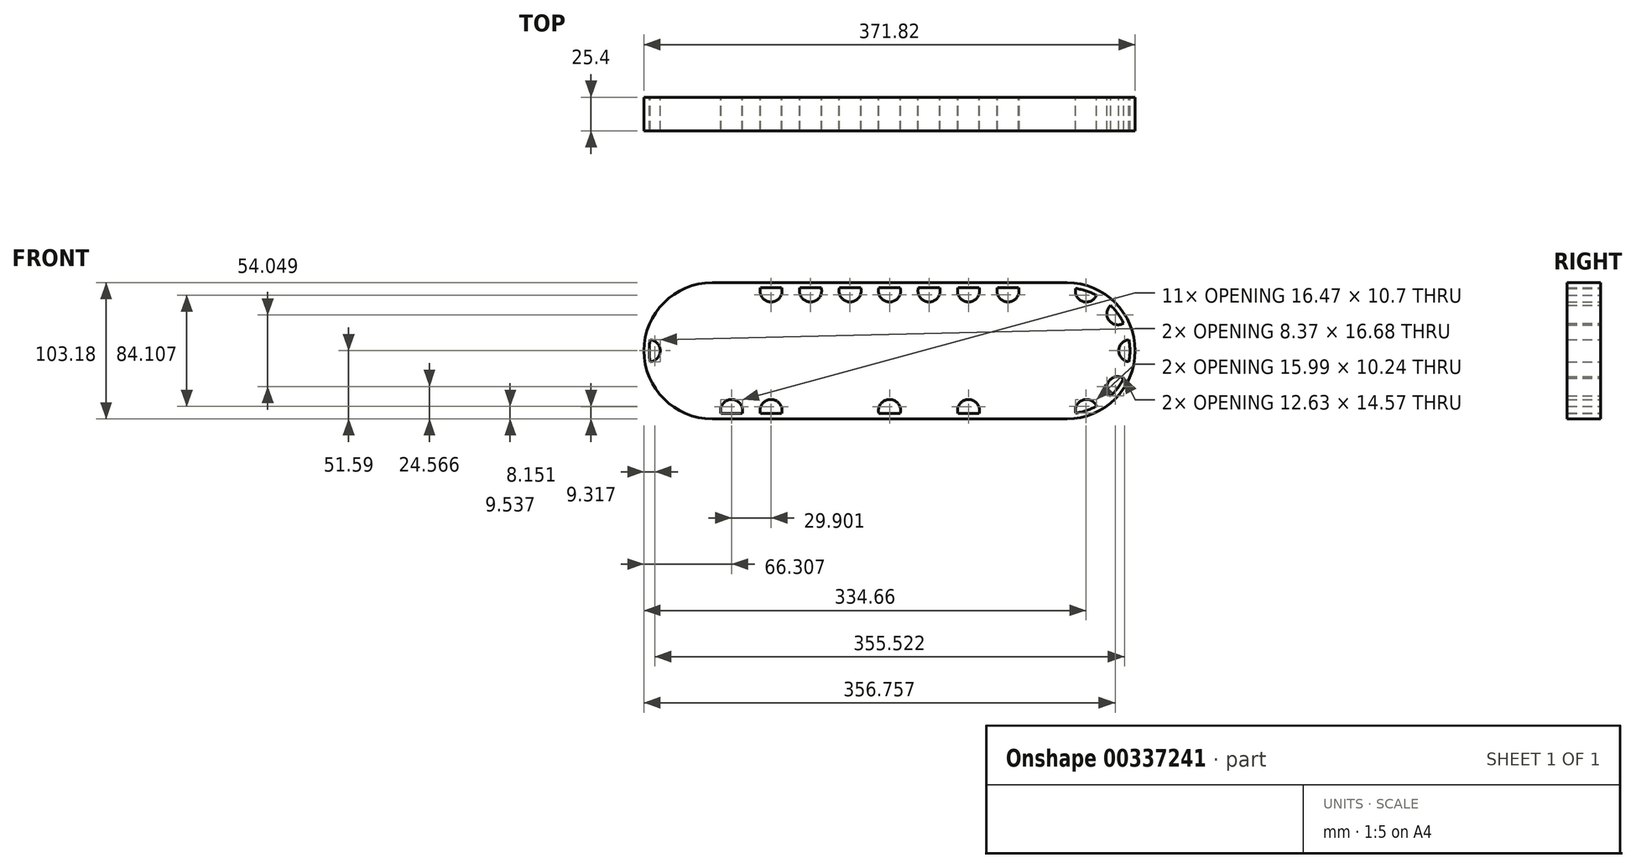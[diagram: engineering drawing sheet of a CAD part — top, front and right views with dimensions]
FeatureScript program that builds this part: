
annotation { "Feature Type Name" : "Feature", "Feature Type Description" : "" }
export const myFeature = defineFeature(function(context is Context, id is Id, definition is map)
    precondition{}
    {
        {
            var Q0;
            Q0=qCreatedBy(makeId("Front.planeOp"),FACE);
            var sketch = newSketch(context, id + "F0", { "sketchPlane" : qUnion([Q0])});
            skCircle(sketch, "E0", {"center": v(0, 0) * mm, "radius": 15.88 * mm});
            skCircle(sketch, "E1", {"center": v(0, 0) * mm, "radius": 25.4 * mm});
            skCircle(sketch, "E2", {"center": v(0, 0) * mm, "radius": 38.1 * mm});
            skArc(sketch, "E3", {"start": v(-23.03, 41.69) * mm, "mid": v(-28, 38.53) * mm, "end": v(-32.53, 34.79) * mm});
            skCircle(sketch, "E4", {"center": v(0, 0) * mm, "radius": 9.53 * mm});
            skLineSegment(sketch, "E5", {"start": v(-7.62, 37.33) * mm, "end": v(-5.87, 47.26) * mm});
            skLineSegment(sketch, "E6", {"start": v(5.87, 47.26) * mm, "end": v(7.62, 37.33) * mm});
            skLineSegment(sketch, "E7.1.0", {"start": v(-28.1, 25.72) * mm, "end": v(-32.53, 34.79) * mm});
            skLineSegment(sketch, "E7.1.1", {"start": v(-23.03, 41.69) * mm, "end": v(-15.78, 34.68) * mm});
            skLineSegment(sketch, "E7.2.0", {"start": v(-37.86, 4.29) * mm, "end": v(-46.76, 9.02) * mm});
            skLineSegment(sketch, "E7.2.1", {"start": v(-43.14, 20.19) * mm, "end": v(-33.15, 18.78) * mm});
            skLineSegment(sketch, "E8.1.3.0", {"start": v(-33.15, -18.78) * mm, "end": v(-43.14, -20.19) * mm});
            skLineSegment(sketch, "E8.3.3.0", {"start": v(-46.76, -9.02) * mm, "end": v(-37.86, -4.29) * mm});
            skLineSegment(sketch, "E8.1.4.0", {"start": v(-15.78, -34.68) * mm, "end": v(-23.03, -41.69) * mm});
            skLineSegment(sketch, "E8.3.4.0", {"start": v(-32.53, -34.79) * mm, "end": v(-28.1, -25.72) * mm});
            skLineSegment(sketch, "E8.1.5.0", {"start": v(7.62, -37.33) * mm, "end": v(5.87, -47.26) * mm});
            skLineSegment(sketch, "E8.3.5.0", {"start": v(-5.87, -47.26) * mm, "end": v(-7.62, -37.33) * mm});
            skLineSegment(sketch, "E8.1.6.0", {"start": v(28.1, -25.72) * mm, "end": v(32.53, -34.79) * mm});
            skLineSegment(sketch, "E8.3.6.0", {"start": v(23.03, -41.69) * mm, "end": v(15.78, -34.68) * mm});
            skLineSegment(sketch, "E8.1.7.0", {"start": v(37.86, -4.29) * mm, "end": v(46.76, -9.02) * mm});
            skLineSegment(sketch, "E8.3.7.0", {"start": v(43.14, -20.19) * mm, "end": v(33.15, -18.78) * mm});
            skLineSegment(sketch, "E8.1.8.0", {"start": v(33.15, 18.78) * mm, "end": v(43.14, 20.19) * mm});
            skLineSegment(sketch, "E8.3.8.0", {"start": v(46.76, 9.02) * mm, "end": v(37.86, 4.29) * mm});
            skLineSegment(sketch, "E8.1.9.0", {"start": v(15.78, 34.68) * mm, "end": v(23.03, 41.69) * mm});
            skLineSegment(sketch, "E8.3.9.0", {"start": v(32.53, 34.79) * mm, "end": v(28.1, 25.72) * mm});
            skArc(sketch, "E9.trimOffspring", {"start": v(5.87, 47.26) * mm, "mid": v(0, 47.63) * mm, "end": v(-5.87, 47.26) * mm});
            skArc(sketch, "E10.trimOffspring", {"start": v(32.53, 34.79) * mm, "mid": v(28, 38.53) * mm, "end": v(23.03, 41.69) * mm});
            skArc(sketch, "E11.trimOffspring", {"start": v(46.76, 9.02) * mm, "mid": v(45.3, 14.72) * mm, "end": v(43.14, 20.19) * mm});
            skArc(sketch, "E12.trimOffspring", {"start": v(43.14, -20.19) * mm, "mid": v(45.3, -14.72) * mm, "end": v(46.76, -9.02) * mm});
            skArc(sketch, "E13.trimOffspring", {"start": v(23.03, -41.69) * mm, "mid": v(28, -38.53) * mm, "end": v(32.53, -34.79) * mm});
            skArc(sketch, "E14.trimOffspring", {"start": v(-5.87, -47.26) * mm, "mid": v(0, -47.63) * mm, "end": v(5.87, -47.26) * mm});
            skArc(sketch, "E15.trimOffspring", {"start": v(-32.53, -34.79) * mm, "mid": v(-28, -38.53) * mm, "end": v(-23.03, -41.69) * mm});
            skArc(sketch, "E16.trimOffspring", {"start": v(-46.76, -9.02) * mm, "mid": v(-45.3, -14.72) * mm, "end": v(-43.14, -20.19) * mm});
            skArc(sketch, "E17.trimOffspring", {"start": v(-43.14, 20.19) * mm, "mid": v(-45.3, 14.72) * mm, "end": v(-46.76, 9.02) * mm});
            skLineSegment(sketch, "E18", {"start": v(-3.98, 25.09) * mm, "end": v(-3.98, 15.37) * mm});
            skLineSegment(sketch, "E19", {"start": v(3.98, 25.09) * mm, "end": v(3.98, 15.37) * mm});
            skLineSegment(sketch, "E20.1.0", {"start": v(-19.74, -15.99) * mm, "end": v(-11.32, -11.13) * mm});
            skLineSegment(sketch, "E20.1.1", {"start": v(-23.71, -9.1) * mm, "end": v(-15.3, -4.24) * mm});
            skLineSegment(sketch, "E20.2.0", {"start": v(23.71, -9.1) * mm, "end": v(15.3, -4.24) * mm});
            skLineSegment(sketch, "E20.2.1", {"start": v(19.74, -15.99) * mm, "end": v(11.32, -11.13) * mm});
            skSolve(sketch);
        }
        {
            var Q0;
            Q0=qCreatedBy(makeId("Front.planeOp"),FACE);
            var sketch = newSketch(context, id + "F1", { "sketchPlane" : qUnion([Q0])});
            skArc(sketch, "E21", {"start": v(23.03, 41.69) * mm, "mid": v(-10.34, 46.49) * mm, "end": v(-38.53, 28) * mm});
            skLineSegment(sketch, "E22.0", {"start": v(15.78, 34.68) * mm, "end": v(23.03, 41.69) * mm, "construction": true});
            skLineSegment(sketch, "E22.1", {"start": v(5.87, 47.26) * mm, "end": v(7.62, 37.33) * mm, "construction": true});
            skLineSegment(sketch, "E22.2", {"start": v(-7.62, 37.33) * mm, "end": v(-5.87, 47.26) * mm, "construction": true});
            skLineSegment(sketch, "E22.3", {"start": v(-23.03, 41.69) * mm, "end": v(-15.78, 34.68) * mm, "construction": true});
            skLineSegment(sketch, "E22.4", {"start": v(-28.1, 25.72) * mm, "end": v(-32.53, 34.79) * mm, "construction": true});
            skLineSegment(sketch, "E22.5", {"start": v(-43.14, 20.19) * mm, "end": v(-33.15, 18.78) * mm, "construction": true});
            skLineSegment(sketch, "E22.6", {"start": v(-37.86, 4.29) * mm, "end": v(-46.76, 9.02) * mm, "construction": true});
            skLineSegment(sketch, "E22.7", {"start": v(-46.76, -9.02) * mm, "end": v(-37.86, -4.29) * mm, "construction": true});
            skCircle(sketch, "E23", {"center": v(14.72, 45.3) * mm, "radius": 8.37 * mm});
            skCircle(sketch, "E24", {"center": v(-14.72, 45.3) * mm, "radius": 8.37 * mm});
            skCircle(sketch, "E25", {"center": v(-38.53, 28) * mm, "radius": 8.37 * mm});
            skCircle(sketch, "E26", {"center": v(-47.62, 0) * mm, "radius": 8.37 * mm});
            skLineSegment(sketch, "E27", {"start": v(-14.72, 45.3) * mm, "end": v(14.72, 45.3) * mm, "construction": true});
            skArc(sketch, "E28.trimOffspring", {"start": v(-42.84, 20.81) * mm, "mid": v(-45.3, 14.72) * mm, "end": v(-46.89, 8.34) * mm});
            skArc(sketch, "E29.trimOffspring", {"start": v(-47.62, 0) * mm, "mid": v(-24.2, -41.02) * mm, "end": v(23.03, -41.69) * mm});
            skLineSegment(sketch, "E30", {"start": v(14.72, 45.3) * mm, "end": v(44.62, 45.3) * mm, "construction": true});
            skLineSegment(sketch, "E31", {"start": v(44.62, 45.3) * mm, "end": v(74.52, 45.3) * mm, "construction": true});
            skLineSegment(sketch, "E32", {"start": v(74.52, 45.3) * mm, "end": v(104.42, 45.3) * mm, "construction": true});
            skLineSegment(sketch, "E33", {"start": v(104.42, 45.3) * mm, "end": v(134.32, 45.3) * mm, "construction": true});
            skCircle(sketch, "E34", {"center": v(44.62, 45.3) * mm, "radius": 8.37 * mm});
            skCircle(sketch, "E35", {"center": v(74.52, 45.3) * mm, "radius": 8.37 * mm});
            skCircle(sketch, "E36", {"center": v(104.42, 45.3) * mm, "radius": 8.37 * mm});
            skCircle(sketch, "E37", {"center": v(134.32, 45.3) * mm, "radius": 8.37 * mm});
            skPoint(sketch, "E38", {"position": v(23.09, 45.3) * mm});
            skPoint(sketch, "E38.positionSnap0", {"position": v(29.67, 45.3) * mm});
            skPoint(sketch, "E39", {"position": v(36.25, 45.3) * mm});
            skLineSegment(sketch, "E40", {"start": v(0, 0) * mm, "end": v(134.32, 0) * mm, "construction": true});
            skLineSegment(sketch, "E41", {"start": v(134.32, 45.3) * mm, "end": v(134.32, 0) * mm, "construction": true});
            skCircle(sketch, "E42.MirrorC", {"center": v(134.32, -45.3) * mm, "radius": 8.37 * mm});
            skCircle(sketch, "E43.MirrorC", {"center": v(104.42, -45.3) * mm, "radius": 8.37 * mm});
            skCircle(sketch, "E44.MirrorC", {"center": v(74.52, -45.3) * mm, "radius": 8.37 * mm});
            skCircle(sketch, "E45.MirrorC", {"center": v(44.62, -45.3) * mm, "radius": 8.37 * mm});
            skCircle(sketch, "E46.MirrorC", {"center": v(14.72, -45.3) * mm, "radius": 8.37 * mm});
            skCircle(sketch, "E47.MirrorC", {"center": v(-14.72, -45.3) * mm, "radius": 8.37 * mm});
            skCircle(sketch, "E48.MirrorC", {"center": v(-38.53, -28) * mm, "radius": 8.37 * mm});
            skCircle(sketch, "E49.MirrorC", {"center": v(164.22, 45.3) * mm, "radius": 8.37 * mm});
            skCircle(sketch, "E50.MirrorC", {"center": v(194.12, 45.3) * mm, "radius": 8.37 * mm});
            skCircle(sketch, "E51.MirrorC", {"center": v(224.03, 45.3) * mm, "radius": 8.37 * mm});
            skCircle(sketch, "E52.MirrorC", {"center": v(253.93, 45.3) * mm, "radius": 8.37 * mm});
            skCircle(sketch, "E53.MirrorC", {"center": v(283.36, 45.3) * mm, "radius": 8.37 * mm});
            skCircle(sketch, "E54.MirrorC", {"center": v(307.17, 28) * mm, "radius": 8.37 * mm});
            skCircle(sketch, "E55.MirrorC", {"center": v(316.27, 0) * mm, "radius": 8.37 * mm});
            skCircle(sketch, "E56.MirrorC", {"center": v(307.17, -28) * mm, "radius": 8.37 * mm});
            skCircle(sketch, "E57.MirrorC", {"center": v(283.36, -45.3) * mm, "radius": 8.37 * mm});
            skCircle(sketch, "E58.MirrorC", {"center": v(253.93, -45.3) * mm, "radius": 8.37 * mm});
            skCircle(sketch, "E59.MirrorC", {"center": v(224.03, -45.3) * mm, "radius": 8.37 * mm});
            skCircle(sketch, "E60.MirrorC", {"center": v(194.12, -45.3) * mm, "radius": 8.37 * mm});
            skCircle(sketch, "E61.MirrorC", {"center": v(164.22, -45.3) * mm, "radius": 8.37 * mm});
            skSolve(sketch);
        }
        {
            var Q0;
            Q0=qCreatedBy(makeId("Front.planeOp"),FACE);
            var sketch = newSketch(context, id + "F2", { "sketchPlane" : qUnion([Q0])});
            skArc(sketch, "E62", {"start": v(0, 47.63) * mm, "mid": v(-47.63, 0) * mm, "end": v(0, -47.63) * mm});
            skLineSegment(sketch, "E63", {"start": v(0, 47.63) * mm, "end": v(268.64, 47.63) * mm});
            skLineSegment(sketch, "E64", {"start": v(0, -47.63) * mm, "end": v(268.64, -47.63) * mm});
            skLineSegment(sketch, "E65.0", {"start": v(0, 0) * mm, "end": v(134.32, 0) * mm, "construction": true});
            skLineSegment(sketch, "E66.0", {"start": v(134.32, 45.3) * mm, "end": v(134.32, 0) * mm, "construction": true});
            skLineSegment(sketch, "E67.MirrorCS", {"start": v(268.64, 0) * mm, "end": v(134.32, 0) * mm, "construction": true});
            skArc(sketch, "E68", {"start": v(268.64, 47.63) * mm, "mid": v(316.27, 0) * mm, "end": v(268.64, -47.63) * mm});
            skArc(sketch, "E69.0", {"start": v(0, 51.59) * mm, "mid": v(-51.59, 0) * mm, "end": v(0, -51.59) * mm});
            skLineSegment(sketch, "E69.1", {"start": v(0, 51.59) * mm, "end": v(268.64, 51.59) * mm});
            skArc(sketch, "E69.2", {"start": v(268.64, 51.59) * mm, "mid": v(320.23, 0) * mm, "end": v(268.64, -51.59) * mm});
            skLineSegment(sketch, "E69.3", {"start": v(0, -51.59) * mm, "end": v(268.64, -51.59) * mm});
            skArc(sketch, "E70.0", {"start": v(-23.04, 46.15) * mm, "mid": v(-12.13, 37.33) * mm, "end": v(-8.49, 50.88) * mm});
            skArc(sketch, "E70.1", {"start": v(9.2, 51.59) * mm, "mid": v(14.72, 36.92) * mm, "end": v(20.24, 51.59) * mm});
            skArc(sketch, "E70.2", {"start": v(39.1, 51.59) * mm, "mid": v(44.62, 36.92) * mm, "end": v(50.14, 51.59) * mm});
            skArc(sketch, "E70.3", {"start": v(69, 51.59) * mm, "mid": v(74.52, 36.92) * mm, "end": v(80.04, 51.59) * mm});
            skArc(sketch, "E70.4", {"start": v(98.9, 51.59) * mm, "mid": v(104.42, 36.92) * mm, "end": v(109.94, 51.59) * mm});
            skArc(sketch, "E70.5", {"start": v(128.8, 51.59) * mm, "mid": v(134.32, 36.92) * mm, "end": v(139.84, 51.59) * mm});
            skArc(sketch, "E70.6", {"start": v(169.74, 51.59) * mm, "mid": v(164.22, 36.92) * mm, "end": v(158.7, 51.59) * mm});
            skArc(sketch, "E70.7", {"start": v(199.65, 51.59) * mm, "mid": v(194.12, 36.92) * mm, "end": v(188.6, 51.59) * mm});
            skArc(sketch, "E70.8", {"start": v(229.55, 51.59) * mm, "mid": v(224.03, 36.92) * mm, "end": v(218.5, 51.59) * mm});
            skArc(sketch, "E70.9", {"start": v(259.45, 51.59) * mm, "mid": v(253.93, 36.92) * mm, "end": v(248.4, 51.59) * mm});
            skArc(sketch, "E70.10", {"start": v(259.45, -51.59) * mm, "mid": v(253.93, -36.92) * mm, "end": v(248.4, -51.59) * mm});
            skArc(sketch, "E70.11", {"start": v(229.55, -51.59) * mm, "mid": v(224.03, -36.92) * mm, "end": v(218.5, -51.59) * mm});
            skArc(sketch, "E70.12", {"start": v(199.65, -51.59) * mm, "mid": v(194.12, -36.92) * mm, "end": v(188.6, -51.59) * mm});
            skArc(sketch, "E70.13", {"start": v(169.74, -51.59) * mm, "mid": v(164.22, -36.92) * mm, "end": v(158.7, -51.59) * mm});
            skArc(sketch, "E70.14", {"start": v(128.8, -51.59) * mm, "mid": v(134.32, -36.92) * mm, "end": v(139.84, -51.59) * mm});
            skArc(sketch, "E70.15", {"start": v(98.9, -51.59) * mm, "mid": v(104.42, -36.92) * mm, "end": v(109.94, -51.59) * mm});
            skArc(sketch, "E70.16", {"start": v(69, -51.59) * mm, "mid": v(74.52, -36.92) * mm, "end": v(80.04, -51.59) * mm});
            skArc(sketch, "E70.17", {"start": v(39.1, -51.59) * mm, "mid": v(44.62, -36.92) * mm, "end": v(50.14, -51.59) * mm});
            skArc(sketch, "E70.18", {"start": v(9.2, -51.59) * mm, "mid": v(14.72, -36.92) * mm, "end": v(20.24, -51.59) * mm});
            skArc(sketch, "E70.19", {"start": v(-23.04, -46.15) * mm, "mid": v(-12.13, -37.33) * mm, "end": v(-8.49, -50.88) * mm});
            skArc(sketch, "E70.20", {"start": v(-45.77, -23.8) * mm, "mid": v(-31.76, -23.07) * mm, "end": v(-36.77, -36.18) * mm});
            skArc(sketch, "E70.21", {"start": v(-51.02, -7.65) * mm, "mid": v(-39.25, 0) * mm, "end": v(-51.02, 7.65) * mm});
            skArc(sketch, "E70.22", {"start": v(-45.77, 23.8) * mm, "mid": v(-31.76, 23.07) * mm, "end": v(-36.77, 36.18) * mm});
            skArc(sketch, "E70.23", {"start": v(291.69, 46.15) * mm, "mid": v(280.77, 37.33) * mm, "end": v(277.13, 50.88) * mm});
            skArc(sketch, "E70.24", {"start": v(319.66, -7.65) * mm, "mid": v(307.9, 0) * mm, "end": v(319.66, 7.65) * mm});
            skArc(sketch, "E70.25", {"start": v(314.42, -23.8) * mm, "mid": v(300.4, -23.07) * mm, "end": v(305.42, -36.18) * mm});
            skArc(sketch, "E70.26", {"start": v(291.69, -46.15) * mm, "mid": v(280.77, -37.33) * mm, "end": v(277.13, -50.88) * mm});
            skArc(sketch, "E70.27", {"start": v(314.42, 23.8) * mm, "mid": v(300.4, 23.07) * mm, "end": v(305.42, 36.18) * mm});
            skSolve(sketch);
        }
        {
            var Q0;
            Q0 = qSketchRegion(id + "F2", true);
            var Q1;
            {var subQ0=sQuery(id+"F2.wireOp",EDGE,"E70.19");var subQ1=sQuery(id+"F2.wireOp",EDGE,"E62");var subQ2=makeQuery(id+"F2.imprint","INTERSECT",VERTEX,{"disambiguationData":[OD(0.0)],"derivedFrom":[subQ1,subQ0]});Q1=makeQuery(id+"F2.imprint","IMPRINT",FACE,{"disambiguationData":[TD([[makeQuery(id+"F2.imprint","IMPRINT",EDGE,{"disambiguationData":[TD([[subQ2,-1.0]])],"derivedFrom":subQ1}),1.0]])]});}
            var Q2;
            {var subQ0=sQuery(id+"F2.wireOp",EDGE,"E70.20");var subQ1=sQuery(id+"F2.wireOp",EDGE,"E62");var subQ2=makeQuery(id+"F2.imprint","INTERSECT",VERTEX,{"disambiguationData":[OD(0.0)],"derivedFrom":[subQ1,subQ0]});Q2=makeQuery(id+"F2.imprint","IMPRINT",FACE,{"disambiguationData":[TD([[makeQuery(id+"F2.imprint","IMPRINT",EDGE,{"disambiguationData":[TD([[subQ2,-1.0]])],"derivedFrom":subQ1}),1.0]])]});}
            var Q3;
            {var subQ0=sQuery(id+"F2.wireOp",EDGE,"E70.18");var subQ1=sQuery(id+"F2.wireOp",EDGE,"E64");var subQ2=makeQuery(id+"F2.imprint","INTERSECT",VERTEX,{"disambiguationData":[OD(0.0)],"derivedFrom":[subQ1,subQ0]});Q3=makeQuery(id+"F2.imprint","IMPRINT",FACE,{"disambiguationData":[TD([[makeQuery(id+"F2.imprint","IMPRINT",EDGE,{"disambiguationData":[TD([[subQ2,-1.0]])],"derivedFrom":subQ1}),1.0]])]});}
            var Q4;
            {var subQ0=sQuery(id+"F2.wireOp",EDGE,"E70.17");var subQ1=sQuery(id+"F2.wireOp",EDGE,"E64");var subQ2=makeQuery(id+"F2.imprint","INTERSECT",VERTEX,{"disambiguationData":[OD(0.0)],"derivedFrom":[subQ1,subQ0]});Q4=makeQuery(id+"F2.imprint","IMPRINT",FACE,{"disambiguationData":[TD([[makeQuery(id+"F2.imprint","IMPRINT",EDGE,{"disambiguationData":[TD([[subQ2,-1.0]])],"derivedFrom":subQ1}),1.0]])]});}
            var Q5;
            {var subQ0=sQuery(id+"F2.wireOp",EDGE,"E70.16");var subQ1=sQuery(id+"F2.wireOp",EDGE,"E64");var subQ2=makeQuery(id+"F2.imprint","INTERSECT",VERTEX,{"disambiguationData":[OD(0.0)],"derivedFrom":[subQ1,subQ0]});Q5=makeQuery(id+"F2.imprint","IMPRINT",FACE,{"disambiguationData":[TD([[makeQuery(id+"F2.imprint","IMPRINT",EDGE,{"disambiguationData":[TD([[subQ2,-1.0]])],"derivedFrom":subQ1}),1.0]])]});}
            var Q6;
            {var subQ0=sQuery(id+"F2.wireOp",EDGE,"E70.15");var subQ1=sQuery(id+"F2.wireOp",EDGE,"E64");var subQ2=makeQuery(id+"F2.imprint","INTERSECT",VERTEX,{"disambiguationData":[OD(0.0)],"derivedFrom":[subQ1,subQ0]});Q6=makeQuery(id+"F2.imprint","IMPRINT",FACE,{"disambiguationData":[TD([[makeQuery(id+"F2.imprint","IMPRINT",EDGE,{"disambiguationData":[TD([[subQ2,-1.0]])],"derivedFrom":subQ1}),1.0]])]});}
            var Q7;
            {var subQ0=sQuery(id+"F2.wireOp",EDGE,"E70.14");var subQ1=sQuery(id+"F2.wireOp",EDGE,"E64");var subQ2=makeQuery(id+"F2.imprint","INTERSECT",VERTEX,{"disambiguationData":[OD(0.0)],"derivedFrom":[subQ1,subQ0]});Q7=makeQuery(id+"F2.imprint","IMPRINT",FACE,{"disambiguationData":[TD([[makeQuery(id+"F2.imprint","IMPRINT",EDGE,{"disambiguationData":[TD([[subQ2,-1.0]])],"derivedFrom":subQ1}),1.0]])]});}
            var Q8;
            {var subQ0=sQuery(id+"F2.wireOp",EDGE,"E70.13");var subQ1=sQuery(id+"F2.wireOp",EDGE,"E64");var subQ2=makeQuery(id+"F2.imprint","INTERSECT",VERTEX,{"disambiguationData":[OD(0.0)],"derivedFrom":[subQ1,subQ0]});Q8=makeQuery(id+"F2.imprint","IMPRINT",FACE,{"disambiguationData":[TD([[makeQuery(id+"F2.imprint","IMPRINT",EDGE,{"disambiguationData":[TD([[subQ2,-1.0]])],"derivedFrom":subQ1}),1.0]])]});}
            var Q9;
            {var subQ0=sQuery(id+"F2.wireOp",EDGE,"E70.12");var subQ1=sQuery(id+"F2.wireOp",EDGE,"E64");var subQ2=makeQuery(id+"F2.imprint","INTERSECT",VERTEX,{"disambiguationData":[OD(0.0)],"derivedFrom":[subQ1,subQ0]});Q9=makeQuery(id+"F2.imprint","IMPRINT",FACE,{"disambiguationData":[TD([[makeQuery(id+"F2.imprint","IMPRINT",EDGE,{"disambiguationData":[TD([[subQ2,-1.0]])],"derivedFrom":subQ1}),1.0]])]});}
            var Q10;
            {var subQ0=sQuery(id+"F2.wireOp",EDGE,"E70.11");var subQ1=sQuery(id+"F2.wireOp",EDGE,"E64");var subQ2=makeQuery(id+"F2.imprint","INTERSECT",VERTEX,{"disambiguationData":[OD(0.0)],"derivedFrom":[subQ1,subQ0]});Q10=makeQuery(id+"F2.imprint","IMPRINT",FACE,{"disambiguationData":[TD([[makeQuery(id+"F2.imprint","IMPRINT",EDGE,{"disambiguationData":[TD([[subQ2,-1.0]])],"derivedFrom":subQ1}),1.0]])]});}
            var Q11;
            {var subQ0=sQuery(id+"F2.wireOp",EDGE,"E70.10");var subQ1=sQuery(id+"F2.wireOp",EDGE,"E64");var subQ2=makeQuery(id+"F2.imprint","INTERSECT",VERTEX,{"disambiguationData":[OD(0.0)],"derivedFrom":[subQ1,subQ0]});Q11=makeQuery(id+"F2.imprint","IMPRINT",FACE,{"disambiguationData":[TD([[makeQuery(id+"F2.imprint","IMPRINT",EDGE,{"disambiguationData":[TD([[subQ2,-1.0]])],"derivedFrom":subQ1}),1.0]])]});}
            var Q12;
            {var subQ0=sQuery(id+"F2.wireOp",EDGE,"E70.26");var subQ1=sQuery(id+"F2.wireOp",EDGE,"E68");var subQ2=makeQuery(id+"F2.imprint","INTERSECT",VERTEX,{"disambiguationData":[OD(0.0)],"derivedFrom":[subQ1,subQ0]});Q12=makeQuery(id+"F2.imprint","IMPRINT",FACE,{"disambiguationData":[TD([[makeQuery(id+"F2.imprint","IMPRINT",EDGE,{"disambiguationData":[TD([[subQ2,-1.0]])],"derivedFrom":subQ1}),-1.0]])]});}
            var Q13;
            {var subQ0=sQuery(id+"F2.wireOp",EDGE,"E70.25");var subQ1=sQuery(id+"F2.wireOp",EDGE,"E68");var subQ2=makeQuery(id+"F2.imprint","INTERSECT",VERTEX,{"disambiguationData":[OD(0.0)],"derivedFrom":[subQ1,subQ0]});Q13=makeQuery(id+"F2.imprint","IMPRINT",FACE,{"disambiguationData":[TD([[makeQuery(id+"F2.imprint","IMPRINT",EDGE,{"disambiguationData":[TD([[subQ2,-1.0]])],"derivedFrom":subQ1}),-1.0]])]});}
            var Q14;
            {var subQ0=sQuery(id+"F2.wireOp",EDGE,"E70.24");var subQ1=sQuery(id+"F2.wireOp",EDGE,"E68");var subQ2=makeQuery(id+"F2.imprint","INTERSECT",VERTEX,{"disambiguationData":[OD(0.0)],"derivedFrom":[subQ1,subQ0]});Q14=makeQuery(id+"F2.imprint","IMPRINT",FACE,{"disambiguationData":[TD([[makeQuery(id+"F2.imprint","IMPRINT",EDGE,{"disambiguationData":[TD([[subQ2,-1.0]])],"derivedFrom":subQ1}),-1.0]])]});}
            var Q15;
            {var subQ0=sQuery(id+"F2.wireOp",EDGE,"E70.27");var subQ1=sQuery(id+"F2.wireOp",EDGE,"E68");var subQ2=makeQuery(id+"F2.imprint","INTERSECT",VERTEX,{"disambiguationData":[OD(0.0)],"derivedFrom":[subQ1,subQ0]});Q15=makeQuery(id+"F2.imprint","IMPRINT",FACE,{"disambiguationData":[TD([[makeQuery(id+"F2.imprint","IMPRINT",EDGE,{"disambiguationData":[TD([[subQ2,-1.0]])],"derivedFrom":subQ1}),-1.0]])]});}
            var Q16;
            {var subQ0=sQuery(id+"F2.wireOp",EDGE,"E70.23");var subQ1=sQuery(id+"F2.wireOp",EDGE,"E68");var subQ2=makeQuery(id+"F2.imprint","INTERSECT",VERTEX,{"disambiguationData":[OD(0.0)],"derivedFrom":[subQ1,subQ0]});Q16=makeQuery(id+"F2.imprint","IMPRINT",FACE,{"disambiguationData":[TD([[makeQuery(id+"F2.imprint","IMPRINT",EDGE,{"disambiguationData":[TD([[subQ2,-1.0]])],"derivedFrom":subQ1}),-1.0]])]});}
            var Q17;
            {var subQ0=sQuery(id+"F2.wireOp",EDGE,"E70.9");var subQ1=sQuery(id+"F2.wireOp",EDGE,"E63");var subQ2=makeQuery(id+"F2.imprint","INTERSECT",VERTEX,{"disambiguationData":[OD(0.0)],"derivedFrom":[subQ1,subQ0]});Q17=makeQuery(id+"F2.imprint","IMPRINT",FACE,{"disambiguationData":[TD([[makeQuery(id+"F2.imprint","IMPRINT",EDGE,{"disambiguationData":[TD([[subQ2,-1.0]])],"derivedFrom":subQ1}),-1.0]])]});}
            var Q18;
            {var subQ0=sQuery(id+"F2.wireOp",EDGE,"E70.8");var subQ1=sQuery(id+"F2.wireOp",EDGE,"E63");var subQ2=makeQuery(id+"F2.imprint","INTERSECT",VERTEX,{"disambiguationData":[OD(0.0)],"derivedFrom":[subQ1,subQ0]});Q18=makeQuery(id+"F2.imprint","IMPRINT",FACE,{"disambiguationData":[TD([[makeQuery(id+"F2.imprint","IMPRINT",EDGE,{"disambiguationData":[TD([[subQ2,-1.0]])],"derivedFrom":subQ1}),-1.0]])]});}
            var Q19;
            {var subQ0=sQuery(id+"F2.wireOp",EDGE,"E70.7");var subQ1=sQuery(id+"F2.wireOp",EDGE,"E63");var subQ2=makeQuery(id+"F2.imprint","INTERSECT",VERTEX,{"disambiguationData":[OD(0.0)],"derivedFrom":[subQ1,subQ0]});Q19=makeQuery(id+"F2.imprint","IMPRINT",FACE,{"disambiguationData":[TD([[makeQuery(id+"F2.imprint","IMPRINT",EDGE,{"disambiguationData":[TD([[subQ2,-1.0]])],"derivedFrom":subQ1}),-1.0]])]});}
            var Q20;
            {var subQ0=sQuery(id+"F2.wireOp",EDGE,"E70.6");var subQ1=sQuery(id+"F2.wireOp",EDGE,"E63");var subQ2=makeQuery(id+"F2.imprint","INTERSECT",VERTEX,{"disambiguationData":[OD(0.0)],"derivedFrom":[subQ1,subQ0]});Q20=makeQuery(id+"F2.imprint","IMPRINT",FACE,{"disambiguationData":[TD([[makeQuery(id+"F2.imprint","IMPRINT",EDGE,{"disambiguationData":[TD([[subQ2,-1.0]])],"derivedFrom":subQ1}),-1.0]])]});}
            var Q21;
            {var subQ0=sQuery(id+"F2.wireOp",EDGE,"E70.5");var subQ1=sQuery(id+"F2.wireOp",EDGE,"E63");var subQ2=makeQuery(id+"F2.imprint","INTERSECT",VERTEX,{"disambiguationData":[OD(0.0)],"derivedFrom":[subQ1,subQ0]});Q21=makeQuery(id+"F2.imprint","IMPRINT",FACE,{"disambiguationData":[TD([[makeQuery(id+"F2.imprint","IMPRINT",EDGE,{"disambiguationData":[TD([[subQ2,-1.0]])],"derivedFrom":subQ1}),-1.0]])]});}
            var Q22;
            {var subQ0=sQuery(id+"F2.wireOp",EDGE,"E70.4");var subQ1=sQuery(id+"F2.wireOp",EDGE,"E63");var subQ2=makeQuery(id+"F2.imprint","INTERSECT",VERTEX,{"disambiguationData":[OD(0.0)],"derivedFrom":[subQ1,subQ0]});Q22=makeQuery(id+"F2.imprint","IMPRINT",FACE,{"disambiguationData":[TD([[makeQuery(id+"F2.imprint","IMPRINT",EDGE,{"disambiguationData":[TD([[subQ2,-1.0]])],"derivedFrom":subQ1}),-1.0]])]});}
            var Q23;
            {var subQ0=sQuery(id+"F2.wireOp",EDGE,"E70.3");var subQ1=sQuery(id+"F2.wireOp",EDGE,"E63");var subQ2=makeQuery(id+"F2.imprint","INTERSECT",VERTEX,{"disambiguationData":[OD(0.0)],"derivedFrom":[subQ1,subQ0]});Q23=makeQuery(id+"F2.imprint","IMPRINT",FACE,{"disambiguationData":[TD([[makeQuery(id+"F2.imprint","IMPRINT",EDGE,{"disambiguationData":[TD([[subQ2,-1.0]])],"derivedFrom":subQ1}),-1.0]])]});}
            var Q24;
            {var subQ0=sQuery(id+"F2.wireOp",EDGE,"E70.2");var subQ1=sQuery(id+"F2.wireOp",EDGE,"E63");var subQ2=makeQuery(id+"F2.imprint","INTERSECT",VERTEX,{"disambiguationData":[OD(0.0)],"derivedFrom":[subQ1,subQ0]});Q24=makeQuery(id+"F2.imprint","IMPRINT",FACE,{"disambiguationData":[TD([[makeQuery(id+"F2.imprint","IMPRINT",EDGE,{"disambiguationData":[TD([[subQ2,-1.0]])],"derivedFrom":subQ1}),-1.0]])]});}
            var Q25;
            {var subQ0=sQuery(id+"F2.wireOp",EDGE,"E70.1");var subQ1=sQuery(id+"F2.wireOp",EDGE,"E63");var subQ2=makeQuery(id+"F2.imprint","INTERSECT",VERTEX,{"disambiguationData":[OD(0.0)],"derivedFrom":[subQ1,subQ0]});Q25=makeQuery(id+"F2.imprint","IMPRINT",FACE,{"disambiguationData":[TD([[makeQuery(id+"F2.imprint","IMPRINT",EDGE,{"disambiguationData":[TD([[subQ2,-1.0]])],"derivedFrom":subQ1}),-1.0]])]});}
            var Q26;
            {var subQ0=sQuery(id+"F2.wireOp",EDGE,"E70.0");var subQ1=sQuery(id+"F2.wireOp",EDGE,"E62");var subQ2=makeQuery(id+"F2.imprint","INTERSECT",VERTEX,{"disambiguationData":[OD(0.0)],"derivedFrom":[subQ1,subQ0]});Q26=makeQuery(id+"F2.imprint","IMPRINT",FACE,{"disambiguationData":[TD([[makeQuery(id+"F2.imprint","IMPRINT",EDGE,{"disambiguationData":[TD([[subQ2,-1.0]])],"derivedFrom":subQ1}),1.0]])]});}
            var Q27;
            {var subQ0=sQuery(id+"F2.wireOp",EDGE,"E70.22");var subQ1=sQuery(id+"F2.wireOp",EDGE,"E62");var subQ2=makeQuery(id+"F2.imprint","INTERSECT",VERTEX,{"disambiguationData":[OD(0.0)],"derivedFrom":[subQ1,subQ0]});Q27=makeQuery(id+"F2.imprint","IMPRINT",FACE,{"disambiguationData":[TD([[makeQuery(id+"F2.imprint","IMPRINT",EDGE,{"disambiguationData":[TD([[subQ2,-1.0]])],"derivedFrom":subQ1}),1.0]])]});}
            var Q28;
            {var subQ0=sQuery(id+"F2.wireOp",EDGE,"E70.21");var subQ1=sQuery(id+"F2.wireOp",EDGE,"E62");var subQ2=makeQuery(id+"F2.imprint","INTERSECT",VERTEX,{"disambiguationData":[OD(0.0)],"derivedFrom":[subQ1,subQ0]});Q28=makeQuery(id+"F2.imprint","IMPRINT",FACE,{"disambiguationData":[TD([[makeQuery(id+"F2.imprint","IMPRINT",EDGE,{"disambiguationData":[TD([[subQ2,-1.0]])],"derivedFrom":subQ1}),1.0]])]});}
            extrude(context, id + "F3", {"entities" : qUnion([Q0, Q1, Q2, Q3, Q4, Q5, Q6, Q7, Q8, Q9, Q10, Q11, Q12, Q13, Q14, Q15, Q16, Q17, Q18, Q19, Q20, Q21, Q22, Q23, Q24, Q25, Q26, Q27, Q28]), "depth" : 25.4 * mm});
        }
    });
